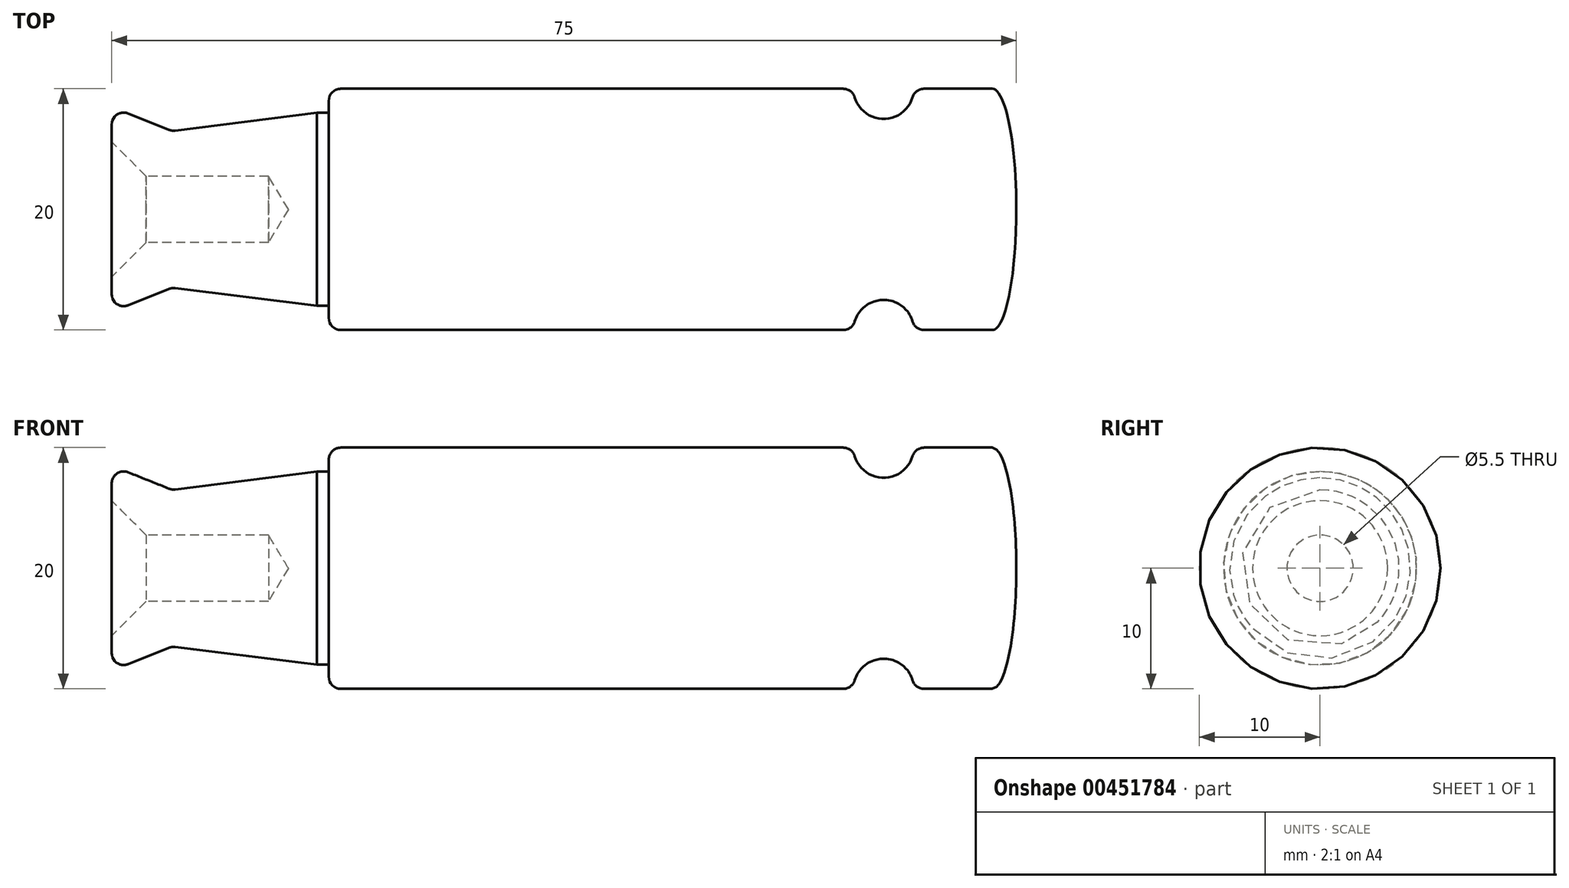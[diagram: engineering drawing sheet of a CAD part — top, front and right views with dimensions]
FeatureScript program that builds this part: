
annotation { "Feature Type Name" : "Feature", "Feature Type Description" : "" }
export const myFeature = defineFeature(function(context is Context, id is Id, definition is map)
    precondition{}
    {
        {
            var Q0;
            Q0=qCreatedBy(makeId("Top.planeOp"),FACE);
            var sketch = newSketch(context, id + "F0", { "sketchPlane" : qUnion([Q0])});
            skLineSegment(sketch, "E0", {"start": v(0, 0) * mm, "end": v(0, 8.5) * mm});
            skLineSegment(sketch, "E1", {"start": v(0, 8.5) * mm, "end": v(5, 6.5) * mm});
            skLineSegment(sketch, "E2", {"start": v(5, 6.5) * mm, "end": v(17, 8) * mm});
            skArc(sketch, "E3", {"start": v(61.5, 10) * mm, "mid": v(64, 7.5) * mm, "end": v(66.5, 10) * mm});
            skLineSegment(sketch, "E4", {"start": v(66.5, 10) * mm, "end": v(73, 10) * mm});
            skEllipticalArc(sketch, "E5", {});
            skLineSegment(sketch, "E6", {"start": v(0, 0) * mm, "end": v(90.2, 0) * mm, "construction": true});
            skPoint(sketch, "E6.endSnap0", {"position": v(75, 0) * mm});
            skLineSegment(sketch, "E7", {"start": v(17, 8) * mm, "end": v(18, 8) * mm});
            skLineSegment(sketch, "E8", {"start": v(18, 8) * mm, "end": v(18, 10) * mm});
            skLineSegment(sketch, "E9", {"start": v(18, 10) * mm, "end": v(61.5, 10) * mm});
            skLineSegment(sketch, "E10", {"start": v(0, 0) * mm, "end": v(75, 0) * mm});
            const initialGuessF0  = {"E5": [0.073, 0, 0, 1, 0.01, 0.002, 4.71238898038469, 0]};
            skSetInitialGuess(sketch, initialGuessF0);
            skSolve(sketch);
        }
        {
            var Q0;
            Q0=makeQuery(id+"F0.imprint","IMPRINT",FACE,{"disambiguationData":[TD([[makeQuery(id+"F0.imprint","IMPRINT",EDGE,{"derivedFrom":sQuery(id+"F0.wireOp",EDGE,"E0")}),-1.0]])]});
            var Q1;
            Q1=sQuery(id+"F0.wireOp",EDGE,"E6");
            revolve(context, id + "F1", {"entities" : qUnion([Q0]), "axis" : qUnion([Q1]), "revolveType" : RevolveType.FULL});
        }
        {
            var Q0;
            Q0=makeQuery(id+"F1.opRevolve","SWEPT_FACE",FACE,{"disambiguationData":[OSD([sQuery(id+"F0.wireOp",EDGE,"E0")])]});
            var sketch = newSketch(context, id + "F2", { "sketchPlane" : qUnion([Q0])});
            skPoint(sketch, "E11", {"position": v(0, 0) * mm});
            skSolve(sketch);
        }
        {
            var Q0;
            Q0=sQuery(id+"F2.wireOp",VERTEX,"E11");
            var Q1;
            Q1=makeQuery(id+"F1.opRevolve","SWEPT_BODY",BODY,{"disambiguationData":[OSD([sQuery(id+"F0.wireOp",EDGE,"E0"),sQuery(id+"F0.wireOp",EDGE,"E1"),sQuery(id+"F0.wireOp",EDGE,"E2"),sQuery(id+"F0.wireOp",EDGE,"E3"),sQuery(id+"F0.wireOp",EDGE,"E4"),sQuery(id+"F0.wireOp",EDGE,"E5"),sQuery(id+"F0.wireOp",EDGE,"E7"),sQuery(id+"F0.wireOp",EDGE,"E8"),sQuery(id+"F0.wireOp",EDGE,"E9"),sQuery(id+"F0.wireOp",EDGE,"E10")])]});
            hole(context, id + "F3", {"style" : HoleStyle.C_SINK, "endStyle" : HoleEndStyle.BLIND, "standardTappedOrClearance" : lookupTablePath({ "standard" : "ISO", "fit" : "Normal", "size" : "M5", "type" : "Clearance" }), "standardBlindInLast" : lookupTablePath({ "fit" : "Standard", "standard" : "ISO", "size" : "M5", "type" : "Clearance" }), "holeDiameter" : 5.5 * mm, "cSinkDiameter" : 11.2 * mm, "cSinkAngle" : 90 * degree, "holeDepth" : 13 * mm, "tappedDepth" : 12 * mm, "tapClearance" : 3, "startFromSketch" : true, "locations" : qUnion([Q0]), "scope" : qUnion([Q1])});
        }
        {
            var Q0;
            Q0=makeQuery(id+"F1.opRevolve","SWEPT_EDGE",EDGE,{"disambiguationData":[OSD([sQuery(id+"F0.wireOp",EDGE,"E1"),sQuery(id+"F0.wireOp",EDGE,"E2")])]});
            var Q1;
            Q1=makeQuery(id+"F1.opRevolve","SWEPT_EDGE",EDGE,{"disambiguationData":[OSD([sQuery(id+"F0.wireOp",EDGE,"E8"),sQuery(id+"F0.wireOp",EDGE,"E9")])]});
            var Q2;
            Q2=makeQuery(id+"F1.opRevolve","SWEPT_EDGE",EDGE,{"disambiguationData":[OSD([sQuery(id+"F0.wireOp",EDGE,"E3"),sQuery(id+"F0.wireOp",EDGE,"E4")])]});
            var Q3;
            Q3=makeQuery(id+"F1.opRevolve","SWEPT_EDGE",EDGE,{"disambiguationData":[OSD([sQuery(id+"F0.wireOp",EDGE,"E3"),sQuery(id+"F0.wireOp",EDGE,"E9")])]});
            var Q4;
            Q4=makeQuery(id+"F1.opRevolve","SWEPT_EDGE",EDGE,{"disambiguationData":[OSD([sQuery(id+"F0.wireOp",EDGE,"E4"),sQuery(id+"F0.wireOp",EDGE,"E5")])]});
            var Q5;
            Q5=makeQuery(id+"F1.opRevolve","SWEPT_EDGE",EDGE,{"disambiguationData":[OSD([sQuery(id+"F0.wireOp",EDGE,"E0"),sQuery(id+"F0.wireOp",EDGE,"E1")])]});
            fillet(context, id + "F4", {"entities" : qUnion([Q0, Q1, Q2, Q3, Q4, Q5]), "radius" : 1 * mm, "tangentPropagation" : true, "allowEdgeOverflow" : false});
        }
    });
